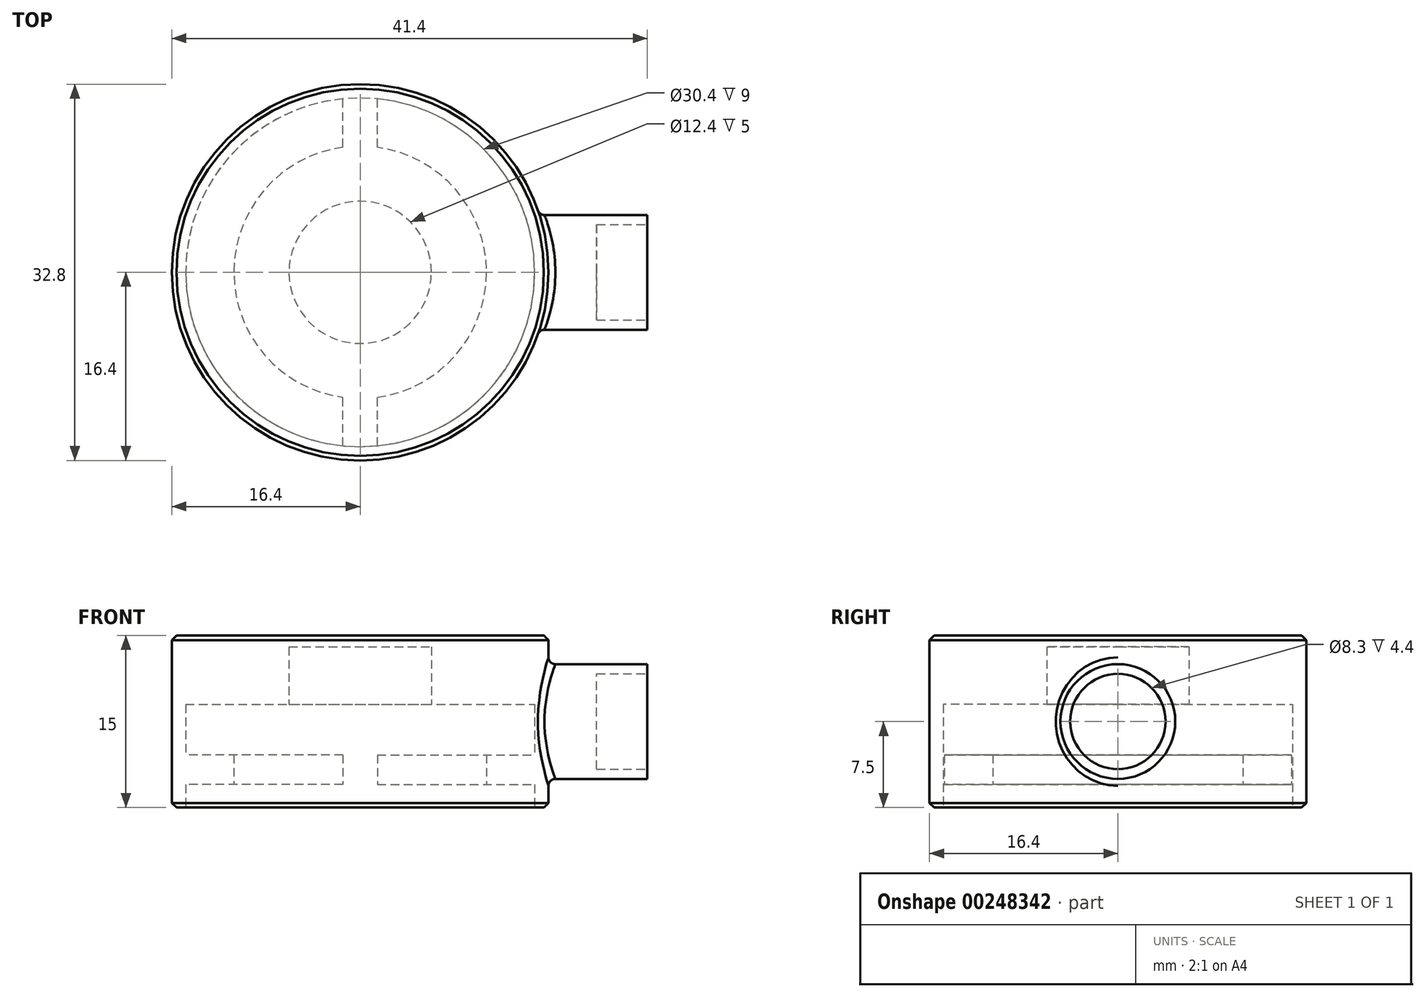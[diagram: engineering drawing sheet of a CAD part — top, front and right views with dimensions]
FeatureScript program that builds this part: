
annotation { "Feature Type Name" : "Feature", "Feature Type Description" : "" }
export const myFeature = defineFeature(function(context is Context, id is Id, definition is map)
    precondition{}
    {
        {
            var Q0;
            Q0=qCreatedBy(makeId("Top.planeOp"),FACE);
            var sketch = newSketch(context, id + "F0", { "sketchPlane" : qUnion([Q0])});
            skCircle(sketch, "E0", {"center": v(0, 0) * mm, "radius": 16.4 * mm});
            skSolve(sketch);
        }
        {
            var Q0;
            Q0 = qSketchRegion(id + "F0", true);
            extrude(context, id + "F1", {"entities" : qUnion([Q0]), "depth" : 15 * mm});
        }
        {
            var Q0;
            Q0=makeQuery(id+"F1.opExtrude","CAP_FACE",FACE,{"disambiguationData":[OSD([sQuery(id+"F0.wireOp",EDGE,"E0")])],"isStart":true});
            var sketch = newSketch(context, id + "F2", { "sketchPlane" : qUnion([Q0])});
            skCircle(sketch, "E1", {"center": v(0, 0) * mm, "radius": 15.2 * mm});
            skSolve(sketch);
        }
        {
            var Q0;
            Q0 = qSketchRegion(id + "F2", true);
            extrude(context, id + "F3", {"entities" : qUnion([Q0]), "operationType" : NewBodyOperationType.REMOVE, "oppositeDirection" : true, "depth" : 2 * mm});
        }
        {
            var Q0;
            Q0=makeQuery(id+"F3.boolean.opBoolean","COPY",FACE,{"derivedFrom":makeQuery(id+"F3.opExtrude","CAP_FACE",FACE,{"disambiguationData":[OSD([sQuery(id+"F2.wireOp",EDGE,"E1")])],"isStart":false})});
            var sketch = newSketch(context, id + "F4", { "sketchPlane" : qUnion([Q0])});
            skCircle(sketch, "E2", {"center": v(0, 0) * mm, "radius": 11 * mm});
            skSolve(sketch);
        }
        {
            var Q0;
            Q0 = qSketchRegion(id + "F4", true);
            extrude(context, id + "F5", {"entities" : qUnion([Q0]), "operationType" : NewBodyOperationType.REMOVE, "oppositeDirection" : true, "depth" : 25 * mm});
        }
        {
            var Q0;
            Q0=makeQuery(id+"F1.opExtrude","CAP_FACE",FACE,{"disambiguationData":[OSD([sQuery(id+"F0.wireOp",EDGE,"E0")])],"isStart":false});
            var sketch = newSketch(context, id + "F6", { "sketchPlane" : qUnion([Q0])});
            skCircle(sketch, "E3", {"center": v(0, 0) * mm, "radius": 15.2 * mm});
            skSolve(sketch);
        }
        {
            var Q0;
            Q0 = qSketchRegion(id + "F6", true);
            extrude(context, id + "F7", {"entities" : qUnion([Q0]), "operationType" : NewBodyOperationType.REMOVE, "oppositeDirection" : true, "depth" : 10.4 * mm});
        }
        {
            var Q0;
            Q0=makeQuery(id+"F1.opExtrude","CAP_FACE",FACE,{"disambiguationData":[OSD([sQuery(id+"F0.wireOp",EDGE,"E0")])],"isStart":false});
            var sketch = newSketch(context, id + "F8", { "sketchPlane" : qUnion([Q0])});
            skCircle(sketch, "E4", {"center": v(0, 0) * mm, "radius": 15.5 * mm});
            skSolve(sketch);
        }
        {
            var Q0;
            Q0 = qSketchRegion(id + "F8", true);
            extrude(context, id + "F9", {"entities" : qUnion([Q0]), "operationType" : NewBodyOperationType.ADD, "oppositeDirection" : true, "depth" : 6 * mm});
        }
        {
            var Q0;
            Q0=makeQuery(id+"F9.opExtrude","CAP_FACE",FACE,{"disambiguationData":[OSD([sQuery(id+"F8.wireOp",EDGE,"E4")])],"isStart":false});
            var sketch = newSketch(context, id + "F10", { "sketchPlane" : qUnion([Q0])});
            skCircle(sketch, "E5", {"center": v(0, 0) * mm, "radius": 6.2 * mm});
            skSolve(sketch);
        }
        {
            var Q0;
            Q0 = qSketchRegion(id + "F10", true);
            extrude(context, id + "F11", {"entities" : qUnion([Q0]), "operationType" : NewBodyOperationType.REMOVE, "oppositeDirection" : true, "depth" : 5 * mm});
        }
        {
            var Q0;
            Q0=makeQuery(id+"F3.boolean.opBoolean","COPY",FACE,{"derivedFrom":makeQuery(id+"F3.opExtrude","CAP_FACE",FACE,{"disambiguationData":[OSD([sQuery(id+"F2.wireOp",EDGE,"E1")])],"isStart":false})});
            var sketch = newSketch(context, id + "F12", { "sketchPlane" : qUnion([Q0])});
            skLineSegment(sketch, "E6.bottom", {"start": v(1.5, 18) * mm, "end": v(-1.5, 18) * mm});
            skLineSegment(sketch, "E6.top", {"start": v(1.5, -18) * mm, "end": v(-1.5, -18) * mm});
            skLineSegment(sketch, "E6.left", {"start": v(1.5, 18) * mm, "end": v(1.5, -18) * mm});
            skLineSegment(sketch, "E6.right", {"start": v(-1.5, 18) * mm, "end": v(-1.5, -18) * mm});
            skPoint(sketch, "E6.middle", {"position": v(0, 0) * mm});
            skCircle(sketch, "E7.0", {"center": v(0, 0) * mm, "radius": 15.2 * mm});
            skSolve(sketch);
        }
        {
            var Q0;
            {var subQ0=sQuery(id+"F12.wireOp",EDGE,"E7.0");var subQ1=sQuery(id+"F12.wireOp",EDGE,"E6.left");var subQ2=makeQuery(id+"F12.imprint","INTERSECT",VERTEX,{"disambiguationData":[OD(0.0)],"derivedFrom":[subQ1,subQ0]});Q0=makeQuery(id+"F12.imprint","IMPRINT",FACE,{"disambiguationData":[TD([[makeQuery(id+"F12.imprint","IMPRINT",EDGE,{"disambiguationData":[TD([[subQ2,-1.0]])],"derivedFrom":subQ1}),-1.0]])]});}
            var Q1;
            {var subQ0=sQuery(id+"F12.wireOp",EDGE,"E7.0");var subQ1=sQuery(id+"F12.wireOp",EDGE,"E6.left");var subQ2=makeQuery(id+"F12.imprint","INTERSECT",VERTEX,{"disambiguationData":[OD(1.0)],"derivedFrom":[subQ1,subQ0]});Q1=makeQuery(id+"F12.imprint","IMPRINT",FACE,{"disambiguationData":[TD([[makeQuery(id+"F12.imprint","IMPRINT",EDGE,{"disambiguationData":[TD([[subQ2,1.0]])],"derivedFrom":subQ1}),-1.0]])]});}
            extrude(context, id + "F13", {"entities" : qUnion([Q0, Q1]), "operationType" : NewBodyOperationType.REMOVE, "oppositeDirection" : true, "depth" : 5 * mm});
        }
        {
            var Q0;
            Q0=qCreatedBy(makeId("Right.planeOp"),FACE);
            var sketch = newSketch(context, id + "F14", { "sketchPlane" : qUnion([Q0])});
            skCircle(sketch, "E8", {"center": v(0, 7.5) * mm, "radius": 5 * mm});
            skSolve(sketch);
        }
        {
            var Q0;
            Q0 = qSketchRegion(id + "F14", true);
            var Q1;
            Q1=makeQuery(id+"F1.opExtrude","SWEPT_BODY",BODY,{"disambiguationData":[OSD([sQuery(id+"F0.wireOp",EDGE,"E0")])]});
            extrude(context, id + "F15", {"entities" : qUnion([Q0]), "operationType" : NewBodyOperationType.ADD, "depth" : 25 * mm, "hasSecondDirection" : true, "secondDirectionBound" : SecondDirectionBoundingType.UP_TO_BODY, "secondDirectionOppositeDirection" : false, "secondDirectionBoundEntityBody" : qUnion([Q1]), "secondDirectionDepth" : 25 * mm});
        }
        {
            var Q0;
            Q0=makeQuery(id+"F15.boolean.opBoolean","INTERSECT",EDGE,{"derivedFrom":[makeQuery(id+"F1.opExtrude","SWEPT_FACE",FACE,{"disambiguationData":[OSD([sQuery(id+"F0.wireOp",EDGE,"E0")])]}),makeQuery(id+"F15.opExtrude","SWEPT_FACE",FACE,{"disambiguationData":[OSD([sQuery(id+"F14.wireOp",EDGE,"E8")])]})]});
            fillet(context, id + "F16", {"entities" : qUnion([Q0]), "radius" : 0.6 * mm, "tangentPropagation" : true, "allowEdgeOverflow" : false});
        }
        {
            var Q0;
            Q0=makeQuery(id+"F1.opExtrude","CAP_EDGE",EDGE,{"disambiguationData":[OSD([sQuery(id+"F0.wireOp",EDGE,"E0")])],"isStart":true});
            var Q1;
            Q1=makeQuery(id+"F1.opExtrude","CAP_EDGE",EDGE,{"disambiguationData":[OSD([sQuery(id+"F0.wireOp",EDGE,"E0")])],"isStart":false});
            chamfer(context, id + "F17", {"entities" : qUnion([Q0, Q1]), "width" : 0.4 * mm, "tangentPropagation" : true});
        }
        {
            var Q0;
            Q0=makeQuery(id+"F15.opExtrude","CAP_FACE",FACE,{"disambiguationData":[OSD([sQuery(id+"F14.wireOp",EDGE,"E8")])],"isStart":false});
            var sketch = newSketch(context, id + "F18", { "sketchPlane" : qUnion([Q0])});
            skCircle(sketch, "E9", {"center": v(0, 7.5) * mm, "radius": 4.15 * mm});
            skSolve(sketch);
        }
        {
            var Q0;
            Q0 = qSketchRegion(id + "F18", true);
            extrude(context, id + "F19", {"entities" : qUnion([Q0]), "operationType" : NewBodyOperationType.REMOVE, "oppositeDirection" : true, "depth" : 4.4 * mm});
        }
    });
